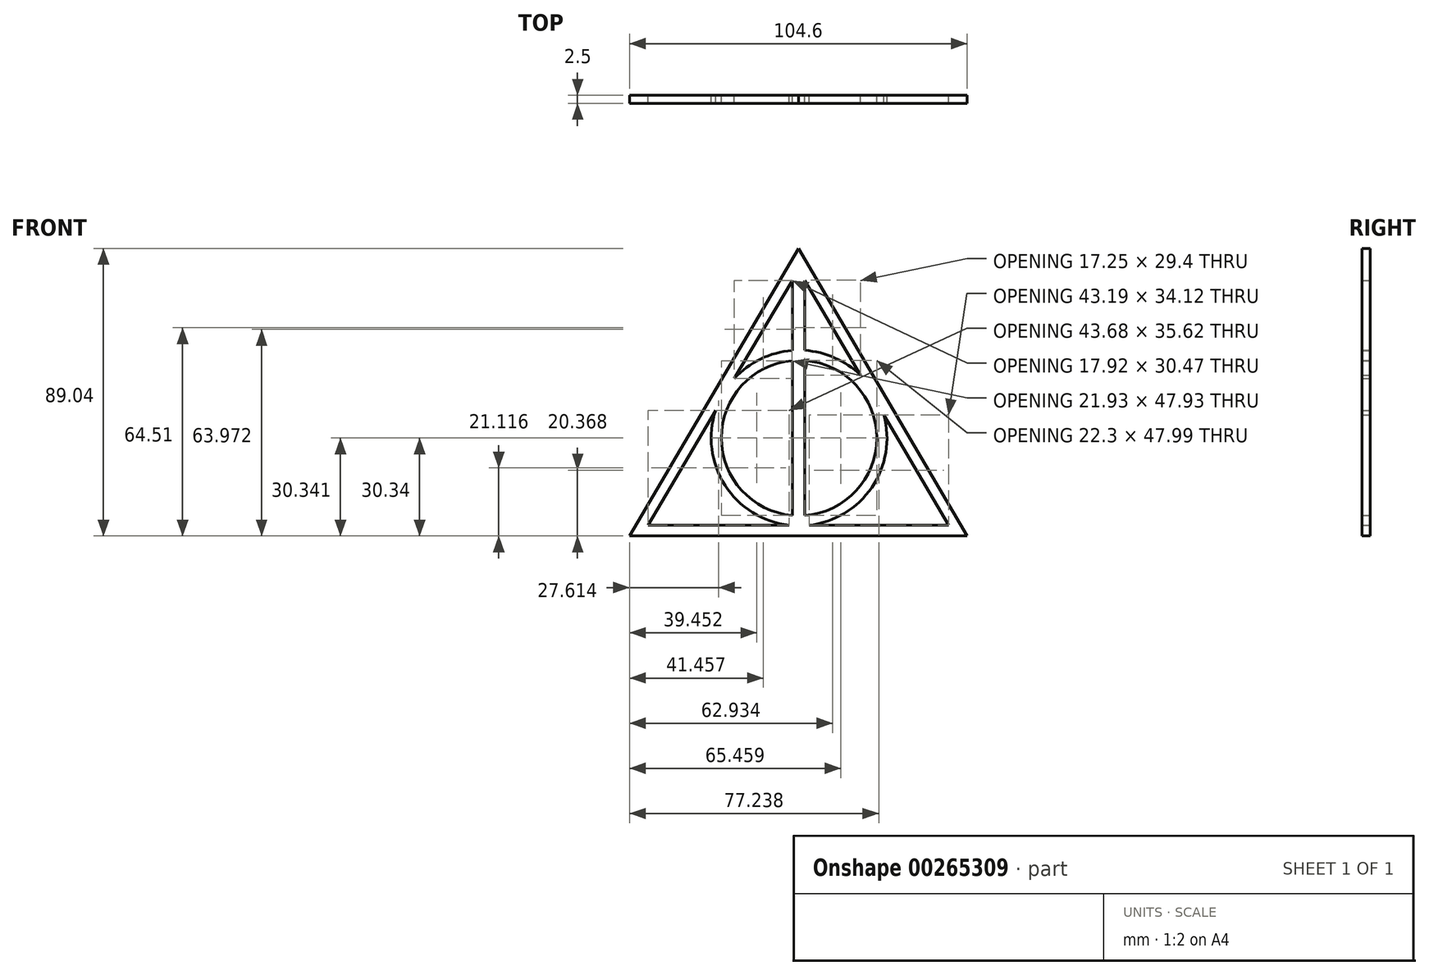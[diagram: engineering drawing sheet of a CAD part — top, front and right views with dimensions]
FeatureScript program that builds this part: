
annotation { "Feature Type Name" : "Feature", "Feature Type Description" : "" }
export const myFeature = defineFeature(function(context is Context, id is Id, definition is map)
    precondition{}
    {
        {
            var Q0;
            Q0=qCreatedBy(makeId("Front.planeOp"),FACE);
            var sketch = newSketch(context, id + "F0", { "sketchPlane" : qUnion([Q0])});
            skLineSegment(sketch, "E0", {"start": v(-9.84, 97.43) * mm, "end": v(-62.2, 8.4) * mm});
            skLineSegment(sketch, "E1", {"start": v(-62.2, 8.4) * mm, "end": v(42.39, 8.4) * mm});
            skLineSegment(sketch, "E2", {"start": v(42.39, 8.4) * mm, "end": v(-9.84, 97.43) * mm});
            skLineSegment(sketch, "E3.0", {"start": v(36.62, 11.7) * mm, "end": v(-9.84, 90.91) * mm});
            skLineSegment(sketch, "E3.1", {"start": v(-56.43, 11.7) * mm, "end": v(36.62, 11.7) * mm});
            skLineSegment(sketch, "E3.2", {"start": v(-9.84, 90.91) * mm, "end": v(-56.43, 11.7) * mm});
            skLineSegment(sketch, "E4", {"start": v(-11.8, 87.6) * mm, "end": v(-11.8, 11.7) * mm});
            skLineSegment(sketch, "E5", {"start": v(-7.9, 87.6) * mm, "end": v(-7.9, 11.7) * mm});
            skArc(sketch, "E6", {"start": v(-35.48, 47.32) * mm, "mid": v(-32.6, 24.1) * mm, "end": v(-12.76, 11.7) * mm});
            skArc(sketch, "E7.0", {"start": v(-11.8, 62.7) * mm, "mid": v(-33.72, 38.73) * mm, "end": v(-11.8, 14.76) * mm});
            skArc(sketch, "E8.trimOffspring", {"start": v(9.35, 58.2) * mm, "mid": v(1.41, 63.59) * mm, "end": v(-7.9, 65.88) * mm});
            skArc(sketch, "E9.trimOffspring", {"start": v(-11.8, 65.86) * mm, "mid": v(-21.58, 63.2) * mm, "end": v(-29.71, 57.13) * mm});
            skArc(sketch, "E10.trimOffspring", {"start": v(-7.9, 14.73) * mm, "mid": v(14.4, 38.73) * mm, "end": v(-7.9, 62.73) * mm});
            skArc(sketch, "E11.trimOffspring", {"start": v(-6.57, 11.7) * mm, "mid": v(12.85, 23.44) * mm, "end": v(16.6, 45.82) * mm});
            skSolve(sketch);
        }
        {
            var Q0;
            Q0=makeQuery(id+"F0.imprint","IMPRINT",FACE,{"disambiguationData":[TD([[makeQuery(id+"F0.imprint","IMPRINT",EDGE,{"derivedFrom":sQuery(id+"F0.wireOp",EDGE,"E0")}),1.0]])]});
            var Q1;
            {var subQ5=sQuery(id+"F0.wireOp",EDGE,"E6");Q1=makeQuery(id+"F0.imprint","IMPRINT",FACE,{"disambiguationData":[TD([[makeQuery(id+"F0.imprint","IMPRINT",EDGE,{"derivedFrom":subQ5}),1.0]])]});}
            var Q2;
            {var subQ4=sQuery(id+"F0.wireOp",EDGE,"E3.0");var subQ11=sQuery(id+"F0.wireOp",EDGE,"E3.2");var subQ12=makeQuery(id+"F0.imprint","INTERSECT",VERTEX,{"derivedFrom":[subQ4,subQ11]});Q2=makeQuery(id+"F0.imprint","IMPRINT",FACE,{"disambiguationData":[TD([[makeQuery(id+"F0.imprint","IMPRINT",EDGE,{"disambiguationData":[TD([[subQ12,1.0]])],"derivedFrom":subQ4}),1.0]])]});}
            var Q3;
            {var subQ5=sQuery(id+"F0.wireOp",EDGE,"E8.trimOffspring");Q3=makeQuery(id+"F0.imprint","IMPRINT",FACE,{"disambiguationData":[TD([[makeQuery(id+"F0.imprint","IMPRINT",EDGE,{"derivedFrom":subQ5}),1.0]])]});}
            extrude(context, id + "F1", {"entities" : qUnion([Q0, Q1, Q2, Q3]), "depth" : 2.5 * mm});
        }
    });
